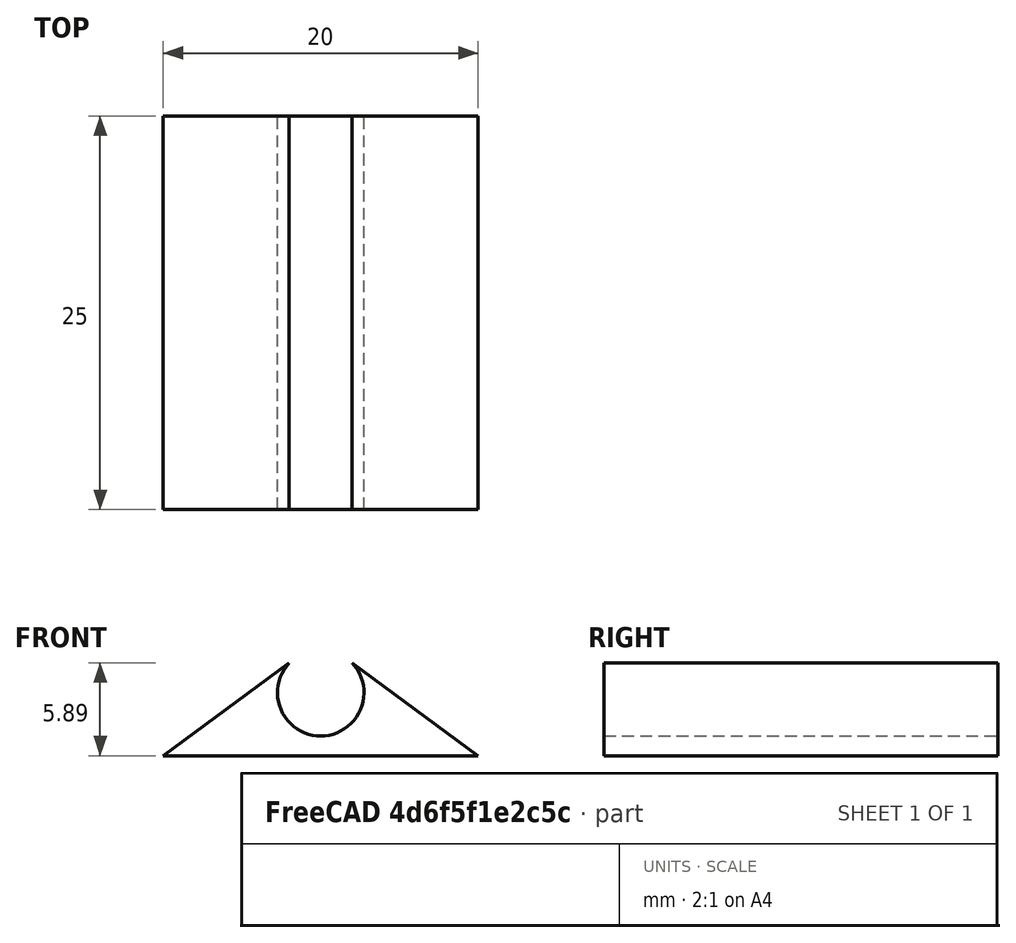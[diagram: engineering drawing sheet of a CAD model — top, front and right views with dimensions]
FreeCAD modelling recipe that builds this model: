
FCSTD DOCUMENT  (FreeCAD 0.20R29603 (Git))
Label: cable floor clip 5mm
License: All rights reserved
LicenseURL: http://en.wikipedia.org/wiki/All_rights_reserved
objects: Sketcher::SketchObject×1, PartDesign::Pad×1, PartDesign::Body×1
note: 4 computed .brp shape members not serialized (recipe doc carries the construction recipe); baked Part::Feature solids carry a one-line shape summary decoded from their .brp

FEATURE [Sketcher::SketchObject] Sketch
  FullyConstrained = true
  MapMode = 5
  Placement = pos=(0,0,0) rot=(1,0,0;1.5708rad)
  Support = -> [XZ_Plane]
  sketch-geometry (4):
    g0: LineSegment StartX=-10 StartY=0 StartZ=0 EndX=10 EndY=0 EndZ=0
    g1: LineSegment StartX=10 StartY=0 StartZ=0 EndX=2 EndY=5.88746 EndZ=0
    g2: LineSegment StartX=-10 StartY=0 StartZ=0 EndX=-2 EndY=5.88746 EndZ=0
    g3: ArcOfCircle CenterX=0 CenterY=4 CenterZ=0 NormalX=0 NormalY=0 NormalZ=1 AngleXU=0 Radius=2.75 StartAngle=2.38514 EndAngle=7.03964
  constraints (12):
    c: PointOnObject(g0,g-1)
    c: Coincident(g0,g1)
    c: Coincident(g0,g2)
    c: Coincident(g3,g2)
    c: Coincident(g3,g1)
    c: DistanceX(g0,g0) = 20
    c: Diameter(g3) = 5.5
    c: PointOnObject(g3,g-2)
    c: Horizontal(g2,g1)
    c: DistanceX(g2,g1) = 4
    c: DistanceY(g-1,g3) = 4
    c: Symmetric(g0,g0,g-1)
FEATURE [PartDesign::Pad] Pad
  Direction = (0,-1,2e-16)
  Length = 25
  Length2 = 10
  Placement = pos=(0,0,0) rot=(1,0,0;1.5708rad)
  Profile = -> Sketch
  ReferenceAxis = -> Sketch [N_Axis]
  Type = 0
FEATURE [PartDesign::Body] Body
  Group = -> [Sketch,Pad]
  Origin = -> Origin
  Tip = -> Pad
